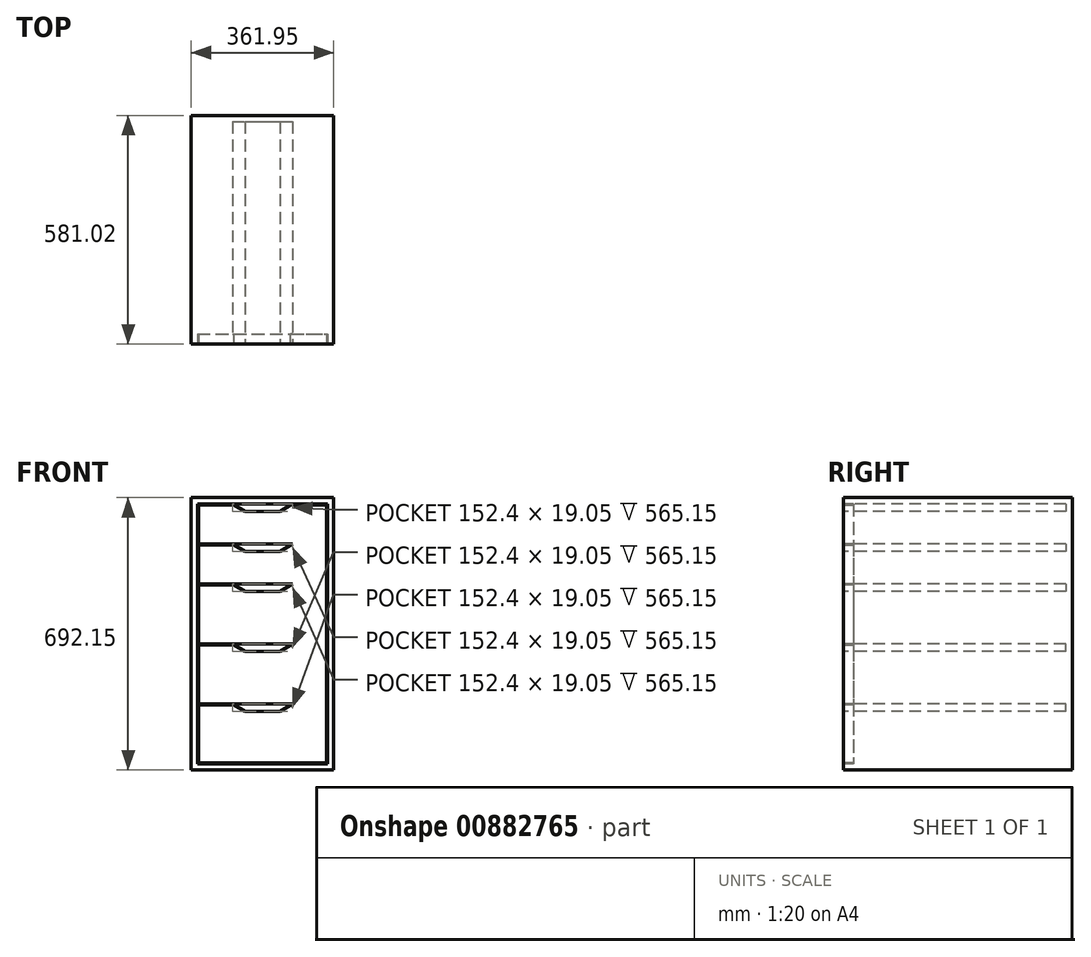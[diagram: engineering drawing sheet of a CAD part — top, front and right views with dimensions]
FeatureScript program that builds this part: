
annotation { "Feature Type Name" : "Feature", "Feature Type Description" : "" }
export const myFeature = defineFeature(function(context is Context, id is Id, definition is map)
    precondition{}
    {
        {
            var Q0;
            Q0=qCreatedBy(makeId("Front.planeOp"),FACE);
            var sketch = newSketch(context, id + "F0", { "sketchPlane" : qUnion([Q0])});
            skLineSegment(sketch, "E0.bottom", {"start": v(0, 0) * mm, "end": v(361.95, 0) * mm});
            skLineSegment(sketch, "E0.top", {"start": v(0, 692.15) * mm, "end": v(361.95, 692.15) * mm});
            skLineSegment(sketch, "E0.left", {"start": v(0, 0) * mm, "end": v(0, 692.15) * mm});
            skLineSegment(sketch, "E0.right", {"start": v(361.95, 0) * mm, "end": v(361.95, 692.15) * mm});
            skSolve(sketch);
        }
        {
            var Q0;
            Q0=qSketchRegion(id+"F0",true);
            extrude(context, id + "F1", {"entities" : qUnion([Q0]), "depth" : 581.02 * mm, "offsetDistance" : 25.4 * mm});
        }
        {
            var Q0;
            Q0=makeQuery(id+"F1.opExtrude","CAP_FACE",FACE,{"disambiguationData":[OSD([sQuery(id+"F0.wireOp",EDGE,"E0.bottom"),sQuery(id+"F0.wireOp",EDGE,"E0.top"),sQuery(id+"F0.wireOp",EDGE,"E0.left"),sQuery(id+"F0.wireOp",EDGE,"E0.right")])],"isStart":false});
            var sketch = newSketch(context, id + "F2", { "sketchPlane" : qUnion([Q0])});
            skLineSegment(sketch, "E1.bottom", {"start": v(15.87, 676.28) * mm, "end": v(346.08, 676.28) * mm});
            skLineSegment(sketch, "E1.top", {"start": v(15.88, 15.88) * mm, "end": v(346.08, 15.88) * mm});
            skLineSegment(sketch, "E1.left", {"start": v(15.87, 676.28) * mm, "end": v(15.88, 15.87) * mm});
            skLineSegment(sketch, "E1.right", {"start": v(346.08, 676.28) * mm, "end": v(346.08, 15.87) * mm});
            skSolve(sketch);
        }
        {
            var Q0;
            Q0=qSketchRegion(id+"F2",true);
            var Q1;
            Q1 = qSketchRegion(id + "F4", true);
            extrude(context, id + "F3", {"entities" : qUnion([Q0, Q1]), "operationType" : NewBodyOperationType.REMOVE, "oppositeDirection" : true, "depth" : 565.15 * mm, "offsetDistance" : 25.4 * mm});
        }
        {
            var Q0;
            Q0=makeQuery(id+"F1.opExtrude","CAP_FACE",FACE,{"disambiguationData":[OSD([sQuery(id+"F0.wireOp",EDGE,"E0.bottom"),sQuery(id+"F0.wireOp",EDGE,"E0.top"),sQuery(id+"F0.wireOp",EDGE,"E0.left"),sQuery(id+"F0.wireOp",EDGE,"E0.right")])],"isStart":false});
            var sketch = newSketch(context, id + "F4", { "sketchPlane" : qUnion([Q0])});
            skLineSegment(sketch, "E2.bottom", {"start": v(15.87, 676.28) * mm, "end": v(346.08, 676.28) * mm});
            skLineSegment(sketch, "E2.top", {"start": v(15.87, 574.68) * mm, "end": v(346.08, 574.68) * mm});
            skLineSegment(sketch, "E2.left", {"start": v(15.87, 676.28) * mm, "end": v(15.87, 574.68) * mm});
            skLineSegment(sketch, "E2.right", {"start": v(346.08, 676.28) * mm, "end": v(346.08, 574.68) * mm});
            skLineSegment(sketch, "E3.top", {"start": v(15.87, 473.08) * mm, "end": v(346.08, 473.08) * mm});
            skLineSegment(sketch, "E3.left", {"start": v(15.87, 574.68) * mm, "end": v(15.87, 473.08) * mm});
            skLineSegment(sketch, "E3.right", {"start": v(346.08, 574.68) * mm, "end": v(346.08, 473.08) * mm});
            skLineSegment(sketch, "E4.top", {"start": v(15.88, 320.68) * mm, "end": v(346.08, 320.68) * mm});
            skLineSegment(sketch, "E4.left", {"start": v(15.87, 473.08) * mm, "end": v(15.87, 320.68) * mm});
            skLineSegment(sketch, "E4.right", {"start": v(346.08, 473.08) * mm, "end": v(346.08, 320.68) * mm});
            skLineSegment(sketch, "E5.top", {"start": v(15.88, 168.28) * mm, "end": v(346.08, 168.28) * mm});
            skLineSegment(sketch, "E5.left", {"start": v(15.87, 320.68) * mm, "end": v(15.87, 168.28) * mm});
            skLineSegment(sketch, "E5.right", {"start": v(346.08, 320.68) * mm, "end": v(346.08, 168.28) * mm});
            skLineSegment(sketch, "E6.top", {"start": v(15.87, 15.87) * mm, "end": v(346.08, 15.87) * mm});
            skLineSegment(sketch, "E6.left", {"start": v(15.87, 168.28) * mm, "end": v(15.87, 15.87) * mm});
            skLineSegment(sketch, "E6.right", {"start": v(346.08, 168.28) * mm, "end": v(346.08, 15.87) * mm});
            skLineSegment(sketch, "E7", {"start": v(104.77, 676.28) * mm, "end": v(136.52, 657.23) * mm});
            skLineSegment(sketch, "E8", {"start": v(225.42, 657.23) * mm, "end": v(257.17, 676.28) * mm});
            skLineSegment(sketch, "E9", {"start": v(257.18, 676.28) * mm, "end": v(225.42, 657.22) * mm});
            skLineSegment(sketch, "E10", {"start": v(136.52, 657.23) * mm, "end": v(225.42, 657.23) * mm});
            skLineSegment(sketch, "E11", {"start": v(257.17, 574.68) * mm, "end": v(225.42, 555.62) * mm});
            skLineSegment(sketch, "E12", {"start": v(225.42, 555.62) * mm, "end": v(136.52, 555.62) * mm});
            skLineSegment(sketch, "E13", {"start": v(136.52, 555.62) * mm, "end": v(104.77, 574.68) * mm});
            skLineSegment(sketch, "E14", {"start": v(104.77, 473.08) * mm, "end": v(136.52, 454.03) * mm});
            skLineSegment(sketch, "E15", {"start": v(136.52, 454.03) * mm, "end": v(225.42, 454.03) * mm});
            skLineSegment(sketch, "E16", {"start": v(225.42, 454.03) * mm, "end": v(257.17, 473.08) * mm});
            skLineSegment(sketch, "E17", {"start": v(257.18, 320.68) * mm, "end": v(225.42, 301.62) * mm});
            skLineSegment(sketch, "E18", {"start": v(225.42, 301.62) * mm, "end": v(136.52, 301.62) * mm});
            skLineSegment(sketch, "E19", {"start": v(136.52, 301.62) * mm, "end": v(104.77, 320.67) * mm});
            skLineSegment(sketch, "E20", {"start": v(104.77, 168.28) * mm, "end": v(136.52, 149.23) * mm});
            skLineSegment(sketch, "E21", {"start": v(136.52, 149.23) * mm, "end": v(225.42, 149.23) * mm});
            skLineSegment(sketch, "E22", {"start": v(225.42, 149.23) * mm, "end": v(257.18, 168.28) * mm});
            skSolve(sketch);
        }
        {
            var Q0;
            Q0=makeQuery(id+"F4.imprint","IMPRINT",FACE,{"disambiguationData":[TD([[makeQuery(id+"F4.imprint","IMPRINT",EDGE,{"derivedFrom":sQuery(id+"F4.wireOp",EDGE,"E6.top")}),1.0]])]});
            var Q1;
            {var subQ2=sQuery(id+"F4.wireOp",EDGE,"E2.left");Q1=makeQuery(id+"F4.imprint","IMPRINT",FACE,{"disambiguationData":[TD([[makeQuery(id+"F4.imprint","IMPRINT",EDGE,{"derivedFrom":subQ2}),1.0]])]});}
            var Q2;
            {var subQ2=sQuery(id+"F4.wireOp",EDGE,"E3.left");Q2=makeQuery(id+"F4.imprint","IMPRINT",FACE,{"disambiguationData":[TD([[makeQuery(id+"F4.imprint","IMPRINT",EDGE,{"derivedFrom":subQ2}),1.0]])]});}
            var Q3;
            {var subQ1=sQuery(id+"F4.wireOp",EDGE,"E4.left");Q3=makeQuery(id+"F4.imprint","IMPRINT",FACE,{"disambiguationData":[TD([[makeQuery(id+"F4.imprint","IMPRINT",EDGE,{"derivedFrom":subQ1}),1.0]])]});}
            var Q4;
            {var subQ1=sQuery(id+"F4.wireOp",EDGE,"E5.left");Q4=makeQuery(id+"F4.imprint","IMPRINT",FACE,{"disambiguationData":[TD([[makeQuery(id+"F4.imprint","IMPRINT",EDGE,{"derivedFrom":subQ1}),1.0]])]});}
            extrude(context, id + "F5", {"entities" : qUnion([Q0, Q1, Q2, Q3, Q4]), "operationType" : NewBodyOperationType.ADD, "oppositeDirection" : true, "depth" : 565.15 * mm, "offsetDistance" : 25.4 * mm});
        }
        {
            var Q0;
            Q0=makeQuery(id+"F5.boolean.opBoolean","MERGE",FACE,{"derivedFrom":[makeQuery(id+"F1.opExtrude","CAP_FACE",FACE,{"disambiguationData":[OSD([sQuery(id+"F0.wireOp",EDGE,"E0.bottom"),sQuery(id+"F0.wireOp",EDGE,"E0.top"),sQuery(id+"F0.wireOp",EDGE,"E0.left"),sQuery(id+"F0.wireOp",EDGE,"E0.right")])],"isStart":false}),makeQuery(id+"F5.opExtrude","CAP_FACE",FACE,{"disambiguationData":[OSD([sQuery(id+"F4.wireOp",EDGE,"E2.bottom"),sQuery(id+"F4.wireOp",EDGE,"E2.left"),sQuery(id+"F4.wireOp",EDGE,"E2.right"),sQuery(id+"F4.wireOp",EDGE,"E2.top"),sQuery(id+"F4.wireOp",EDGE,"E3.left"),sQuery(id+"F4.wireOp",EDGE,"E3.right"),sQuery(id+"F4.wireOp",EDGE,"E3.top"),sQuery(id+"F4.wireOp",EDGE,"E4.left"),sQuery(id+"F4.wireOp",EDGE,"E4.right"),sQuery(id+"F4.wireOp",EDGE,"E4.top"),sQuery(id+"F4.wireOp",EDGE,"E5.left"),sQuery(id+"F4.wireOp",EDGE,"E5.right"),sQuery(id+"F4.wireOp",EDGE,"E5.top"),sQuery(id+"F4.wireOp",EDGE,"E6.top"),sQuery(id+"F4.wireOp",EDGE,"E6.left"),sQuery(id+"F4.wireOp",EDGE,"E6.right"),sQuery(id+"F4.wireOp",EDGE,"E7"),sQuery(id+"F4.wireOp",EDGE,"E9"),sQuery(id+"F4.wireOp",EDGE,"E10"),sQuery(id+"F4.wireOp",EDGE,"E11"),sQuery(id+"F4.wireOp",EDGE,"E12"),sQuery(id+"F4.wireOp",EDGE,"E13"),sQuery(id+"F4.wireOp",EDGE,"E14"),sQuery(id+"F4.wireOp",EDGE,"E15"),sQuery(id+"F4.wireOp",EDGE,"E16"),sQuery(id+"F4.wireOp",EDGE,"E17"),sQuery(id+"F4.wireOp",EDGE,"E18"),sQuery(id+"F4.wireOp",EDGE,"E19"),sQuery(id+"F4.wireOp",EDGE,"E20"),sQuery(id+"F4.wireOp",EDGE,"E21"),sQuery(id+"F4.wireOp",EDGE,"E22")])],"isStart":true})]});
            var sketch = newSketch(context, id + "F6", { "sketchPlane" : qUnion([Q0])});
            skLineSegment(sketch, "E23.bottom", {"start": v(15.87, 676.28) * mm, "end": v(346.08, 676.28) * mm});
            skLineSegment(sketch, "E23.top", {"start": v(15.88, 15.88) * mm, "end": v(346.08, 15.88) * mm});
            skLineSegment(sketch, "E23.left", {"start": v(15.87, 676.28) * mm, "end": v(15.88, 15.88) * mm});
            skLineSegment(sketch, "E23.right", {"start": v(346.08, 676.28) * mm, "end": v(346.08, 15.88) * mm});
            skLineSegment(sketch, "E24.bottom", {"start": v(18.41, 673.74) * mm, "end": v(343.53, 673.74) * mm});
            skLineSegment(sketch, "E24.top", {"start": v(18.42, 18.41) * mm, "end": v(343.54, 18.42) * mm});
            skLineSegment(sketch, "E24.left", {"start": v(18.41, 673.74) * mm, "end": v(18.42, 18.41) * mm});
            skLineSegment(sketch, "E24.right", {"start": v(343.53, 673.74) * mm, "end": v(343.54, 18.42) * mm});
            skLineSegment(sketch, "E25", {"start": v(104.77, 168.28) * mm, "end": v(18.42, 168.28) * mm});
            skLineSegment(sketch, "E26", {"start": v(18.42, 168.28) * mm, "end": v(18.42, 165.73) * mm});
            skLineSegment(sketch, "E27", {"start": v(18.42, 165.73) * mm, "end": v(343.54, 165.74) * mm});
            skLineSegment(sketch, "E28", {"start": v(343.54, 165.74) * mm, "end": v(343.54, 168.28) * mm});
            skLineSegment(sketch, "E29", {"start": v(343.54, 168.28) * mm, "end": v(108.45, 168.28) * mm});
            skLineSegment(sketch, "E30", {"start": v(108.45, 168.28) * mm, "end": v(104.77, 168.28) * mm});
            skLineSegment(sketch, "E31", {"start": v(104.77, 320.68) * mm, "end": v(18.42, 320.68) * mm});
            skLineSegment(sketch, "E32", {"start": v(18.42, 320.68) * mm, "end": v(18.42, 318.14) * mm});
            skLineSegment(sketch, "E33", {"start": v(18.41, 318.14) * mm, "end": v(343.54, 318.14) * mm});
            skLineSegment(sketch, "E34", {"start": v(343.54, 318.14) * mm, "end": v(343.54, 320.68) * mm});
            skLineSegment(sketch, "E35", {"start": v(343.54, 320.68) * mm, "end": v(104.77, 320.68) * mm});
            skLineSegment(sketch, "E36", {"start": v(104.77, 473.08) * mm, "end": v(18.41, 473.08) * mm});
            skLineSegment(sketch, "E37", {"start": v(18.41, 473.08) * mm, "end": v(18.41, 470.54) * mm});
            skLineSegment(sketch, "E38", {"start": v(18.41, 470.54) * mm, "end": v(343.53, 470.54) * mm});
            skLineSegment(sketch, "E39", {"start": v(343.53, 470.54) * mm, "end": v(343.53, 473.08) * mm});
            skLineSegment(sketch, "E40", {"start": v(343.53, 473.08) * mm, "end": v(104.77, 473.08) * mm});
            skLineSegment(sketch, "E41", {"start": v(104.77, 574.68) * mm, "end": v(18.41, 574.68) * mm});
            skLineSegment(sketch, "E42", {"start": v(18.41, 574.68) * mm, "end": v(18.41, 572.13) * mm});
            skLineSegment(sketch, "E43", {"start": v(18.41, 572.13) * mm, "end": v(343.53, 572.14) * mm});
            skLineSegment(sketch, "E44", {"start": v(343.53, 572.14) * mm, "end": v(343.53, 574.68) * mm});
            skLineSegment(sketch, "E45", {"start": v(343.53, 574.68) * mm, "end": v(104.77, 574.68) * mm});
            skSolve(sketch);
        }
        {
            var Q0;
            {var subQ0=sQuery(id+"F6.wireOp",EDGE,"E23.bottom");var subQ1=makeQuery(id+"F5.opExtrude","CAP_EDGE",EDGE,{"disambiguationData":[OSD([sQuery(id+"F4.wireOp",EDGE,"E7")])],"isStart":true});var subQ2=makeQuery(id+"F6.imprint","INTERSECT",VERTEX,{"derivedFrom":[subQ1,subQ0]});Q0=makeQuery(id+"F6.imprint","IMPRINT",FACE,{"disambiguationData":[TD([[makeQuery(id+"F6.imprint","IMPRINT",EDGE,{"disambiguationData":[TD([[subQ2,-1.0]])],"derivedFrom":subQ0}),-1.0]])]});}
            var Q1;
            Q1=makeQuery(id+"F6.imprint","IMPRINT",FACE,{"disambiguationData":[TD([[makeQuery(id+"F6.imprint","IMPRINT",EDGE,{"derivedFrom":sQuery(id+"F6.wireOp",EDGE,"E23.top")}),1.0]])]});
            var Q2;
            {var subQ0=sQuery(id+"F6.wireOp",EDGE,"E43");var subQ1=makeQuery(id+"F5.opExtrude","CAP_EDGE",EDGE,{"disambiguationData":[OSD([sQuery(id+"F4.wireOp",EDGE,"E13")])],"isStart":true});var subQ2=makeQuery(id+"F6.imprint","INTERSECT",VERTEX,{"derivedFrom":[subQ1,subQ0]});Q2=makeQuery(id+"F6.imprint","IMPRINT",FACE,{"disambiguationData":[TD([[makeQuery(id+"F6.imprint","IMPRINT",EDGE,{"disambiguationData":[TD([[subQ2,-1.0]])],"derivedFrom":subQ0}),1.0]])]});}
            var Q3;
            {var subQ0=sQuery(id+"F6.wireOp",EDGE,"E41");Q3=makeQuery(id+"F6.imprint","IMPRINT",FACE,{"disambiguationData":[TD([[makeQuery(id+"F6.imprint","IMPRINT",EDGE,{"derivedFrom":subQ0}),1.0]])]});}
            var Q4;
            {var subQ0=sQuery(id+"F6.wireOp",EDGE,"E44");Q4=makeQuery(id+"F6.imprint","IMPRINT",FACE,{"disambiguationData":[TD([[makeQuery(id+"F6.imprint","IMPRINT",EDGE,{"derivedFrom":subQ0}),1.0]])]});}
            var Q5;
            {var subQ0=sQuery(id+"F6.wireOp",EDGE,"E39");Q5=makeQuery(id+"F6.imprint","IMPRINT",FACE,{"disambiguationData":[TD([[makeQuery(id+"F6.imprint","IMPRINT",EDGE,{"derivedFrom":subQ0}),1.0]])]});}
            var Q6;
            {var subQ0=sQuery(id+"F6.wireOp",EDGE,"E38");var subQ1=makeQuery(id+"F5.opExtrude","CAP_EDGE",EDGE,{"disambiguationData":[OSD([sQuery(id+"F4.wireOp",EDGE,"E14")])],"isStart":true});var subQ2=makeQuery(id+"F6.imprint","INTERSECT",VERTEX,{"derivedFrom":[subQ1,subQ0]});Q6=makeQuery(id+"F6.imprint","IMPRINT",FACE,{"disambiguationData":[TD([[makeQuery(id+"F6.imprint","IMPRINT",EDGE,{"disambiguationData":[TD([[subQ2,-1.0]])],"derivedFrom":subQ0}),1.0]])]});}
            var Q7;
            {var subQ0=sQuery(id+"F6.wireOp",EDGE,"E36");Q7=makeQuery(id+"F6.imprint","IMPRINT",FACE,{"disambiguationData":[TD([[makeQuery(id+"F6.imprint","IMPRINT",EDGE,{"derivedFrom":subQ0}),1.0]])]});}
            var Q8;
            {var subQ0=sQuery(id+"F6.wireOp",EDGE,"E33");var subQ1=makeQuery(id+"F5.opExtrude","CAP_EDGE",EDGE,{"disambiguationData":[OSD([sQuery(id+"F4.wireOp",EDGE,"E19")])],"isStart":true});var subQ2=makeQuery(id+"F6.imprint","INTERSECT",VERTEX,{"derivedFrom":[subQ1,subQ0]});Q8=makeQuery(id+"F6.imprint","IMPRINT",FACE,{"disambiguationData":[TD([[makeQuery(id+"F6.imprint","IMPRINT",EDGE,{"disambiguationData":[TD([[subQ2,-1.0]])],"derivedFrom":subQ0}),1.0]])]});}
            var Q9;
            {var subQ0=sQuery(id+"F6.wireOp",EDGE,"E31");Q9=makeQuery(id+"F6.imprint","IMPRINT",FACE,{"disambiguationData":[TD([[makeQuery(id+"F6.imprint","IMPRINT",EDGE,{"derivedFrom":subQ0}),1.0]])]});}
            var Q10;
            {var subQ0=sQuery(id+"F6.wireOp",EDGE,"E34");Q10=makeQuery(id+"F6.imprint","IMPRINT",FACE,{"disambiguationData":[TD([[makeQuery(id+"F6.imprint","IMPRINT",EDGE,{"derivedFrom":subQ0}),1.0]])]});}
            var Q11;
            {var subQ0=sQuery(id+"F6.wireOp",EDGE,"E28");Q11=makeQuery(id+"F6.imprint","IMPRINT",FACE,{"disambiguationData":[TD([[makeQuery(id+"F6.imprint","IMPRINT",EDGE,{"derivedFrom":subQ0}),1.0]])]});}
            var Q12;
            {var subQ3=sQuery(id+"F6.wireOp",EDGE,"E30");Q12=makeQuery(id+"F6.imprint","IMPRINT",FACE,{"disambiguationData":[TD([[makeQuery(id+"F6.imprint","IMPRINT",EDGE,{"derivedFrom":subQ3}),-1.0]])]});}
            var Q13;
            {var subQ0=sQuery(id+"F6.wireOp",EDGE,"E25");Q13=makeQuery(id+"F6.imprint","IMPRINT",FACE,{"disambiguationData":[TD([[makeQuery(id+"F6.imprint","IMPRINT",EDGE,{"derivedFrom":subQ0}),1.0]])]});}
            extrude(context, id + "F7", {"entities" : qUnion([Q0, Q1, Q2, Q3, Q4, Q5, Q6, Q7, Q8, Q9, Q10, Q11, Q12, Q13]), "operationType" : NewBodyOperationType.REMOVE, "oppositeDirection" : true, "depth" : 25.4 * mm, "offsetDistance" : 25.4 * mm});
        }
    });
